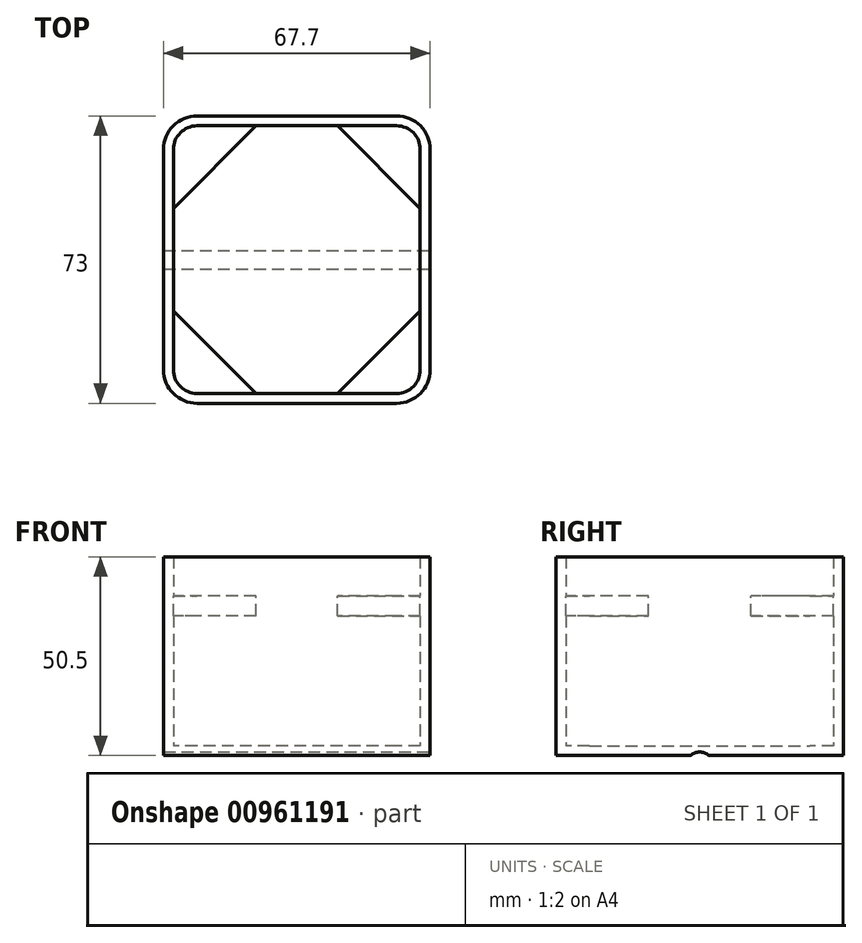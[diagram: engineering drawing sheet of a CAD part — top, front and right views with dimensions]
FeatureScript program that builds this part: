
annotation { "Feature Type Name" : "Feature", "Feature Type Description" : "" }
export const myFeature = defineFeature(function(context is Context, id is Id, definition is map)
    precondition{}
    {
        {
            var Q0;
            Q0=qCreatedBy(makeId("Top.planeOp"),FACE);
            var sketch = newSketch(context, id + "F0", { "sketchPlane" : qUnion([Q0])});
            skLineSegment(sketch, "E0.bottom", {"start": v(25.35, -36.5) * mm, "end": v(-25.35, -36.5) * mm});
            skLineSegment(sketch, "E0.top", {"start": v(25.35, 36.5) * mm, "end": v(-25.35, 36.5) * mm});
            skLineSegment(sketch, "E0.left", {"start": v(33.85, -28) * mm, "end": v(33.85, 28) * mm});
            skLineSegment(sketch, "E0.right", {"start": v(-33.85, -28) * mm, "end": v(-33.85, 28) * mm});
            skPoint(sketch, "E0.middle", {"position": v(0, 0) * mm});
            skPoint(sketch, "E1.visualSharp", {"position": v(-33.85, 36.5) * mm});
            skPoint(sketch, "E2.visualSharp", {"position": v(33.85, 36.5) * mm});
            skPoint(sketch, "E3.visualSharp", {"position": v(33.85, -36.5) * mm});
            skPoint(sketch, "E4.visualSharp", {"position": v(-33.85, -36.5) * mm});
            skArc(sketch, "E5.filletArc", {"start": v(-25.35, 36.5) * mm, "mid": v(-31.36, 34.01) * mm, "end": v(-33.85, 28) * mm});
            skArc(sketch, "E6.filletArc", {"start": v(33.85, 28) * mm, "mid": v(31.36, 34.01) * mm, "end": v(25.35, 36.5) * mm});
            skArc(sketch, "E7.filletArc", {"start": v(-33.85, -28) * mm, "mid": v(-31.36, -34.01) * mm, "end": v(-25.35, -36.5) * mm});
            skArc(sketch, "E8.filletArc", {"start": v(25.35, -36.5) * mm, "mid": v(31.36, -34.01) * mm, "end": v(33.85, -28) * mm});
            skSolve(sketch);
        }
        {
            var Q0;
            Q0=makeQuery(id+"F0.imprint","IMPRINT",FACE,{"disambiguationData":[TD([[makeQuery(id+"F0.imprint","IMPRINT",EDGE,{"derivedFrom":sQuery(id+"F0.wireOp",EDGE,"E0.bottom")}),-1.0]])]});
            extrude(context, id + "F1", {"entities" : qUnion([Q0]), "depth" : 2.5 * mm, "offsetDistance" : 25 * mm});
        }
        {
            var Q0;
            Q0=makeQuery(id+"F1.opExtrude","CAP_FACE",FACE,{"disambiguationData":[OSD([sQuery(id+"F0.wireOp",EDGE,"E0.bottom"),sQuery(id+"F0.wireOp",EDGE,"E0.top"),sQuery(id+"F0.wireOp",EDGE,"E0.left"),sQuery(id+"F0.wireOp",EDGE,"E0.right"),sQuery(id+"F0.wireOp",EDGE,"E1.filletArc"),sQuery(id+"F0.wireOp",EDGE,"E2.filletArc"),sQuery(id+"F0.wireOp",EDGE,"E3.filletArc"),sQuery(id+"F0.wireOp",EDGE,"E4.filletArc")])],"isStart":false});
            var sketch = newSketch(context, id + "F2", { "sketchPlane" : qUnion([Q0])});
            skLineSegment(sketch, "E9.bottom", {"start": v(25.35, -34) * mm, "end": v(-25.35, -34) * mm});
            skLineSegment(sketch, "E9.top", {"start": v(25.35, 34) * mm, "end": v(-25.35, 34) * mm});
            skLineSegment(sketch, "E9.left", {"start": v(31.35, -28) * mm, "end": v(31.35, 28) * mm});
            skLineSegment(sketch, "E9.right", {"start": v(-31.35, -28) * mm, "end": v(-31.35, 28) * mm});
            skPoint(sketch, "E9.middle", {"position": v(0, 0) * mm});
            skPoint(sketch, "E10.visualSharp", {"position": v(-31.35, 34) * mm});
            skPoint(sketch, "E11.visualSharp", {"position": v(31.35, 34) * mm});
            skPoint(sketch, "E12.visualSharp", {"position": v(-31.35, -34) * mm});
            skPoint(sketch, "E13.visualSharp", {"position": v(31.35, -34) * mm});
            skPoint(sketch, "E14", {"position": v(-22.35, 25) * mm});
            skPoint(sketch, "E15", {"position": v(22.35, 25) * mm});
            skPoint(sketch, "E16", {"position": v(22.35, -25) * mm});
            skPoint(sketch, "E17", {"position": v(-22.35, -25) * mm});
            skArc(sketch, "E18.filletArc", {"start": v(-25.35, 34) * mm, "mid": v(-29.6, 32.24) * mm, "end": v(-31.35, 28) * mm});
            skArc(sketch, "E19.filletArc", {"start": v(31.35, 28) * mm, "mid": v(29.6, 32.24) * mm, "end": v(25.35, 34) * mm});
            skArc(sketch, "E20.filletArc", {"start": v(25.35, -34) * mm, "mid": v(29.6, -32.24) * mm, "end": v(31.35, -28) * mm});
            skArc(sketch, "E21.filletArc", {"start": v(-31.35, -28) * mm, "mid": v(-29.6, -32.24) * mm, "end": v(-25.35, -34) * mm});
            skSolve(sketch);
        }
        {
            var Q0;
            Q0=makeQuery(id+"F2.imprint","IMPRINT",FACE,{"disambiguationData":[TD([[makeQuery(id+"F2.imprint","IMPRINT",EDGE,{"derivedFrom":sQuery(id+"F2.wireOp",EDGE,"E9.bottom")}),1.0]])]});
            extrude(context, id + "F3", {"entities" : qUnion([Q0]), "operationType" : NewBodyOperationType.ADD, "depth" : 38 * mm, "offsetDistance" : 25 * mm});
        }
        {
            var Q0;
            Q0=makeQuery(id+"F3.opExtrude","CAP_FACE",FACE,{"disambiguationData":[OSD([sQuery(id+"F0.wireOp",EDGE,"E0.bottom"),sQuery(id+"F0.wireOp",EDGE,"E0.top"),sQuery(id+"F0.wireOp",EDGE,"E0.left"),sQuery(id+"F0.wireOp",EDGE,"E0.right"),sQuery(id+"F0.wireOp",EDGE,"dvduAT8U-9z4F-e4AS-9eoL-lbGmKiJ1iybt"),sQuery(id+"F0.wireOp",EDGE,"aJOZrvJK-A2hF-QCfp-oE2e-V53GVGUSBUPk"),sQuery(id+"F0.wireOp",EDGE,"IG0yzDuE-LkIn-5tUI-d1jc-H29fERG7UsIG"),sQuery(id+"F0.wireOp",EDGE,"B1HQ0swq-clk5-EkSq-0daU-o4C5Dgl36Lca"),sQuery(id+"F0.wireOp",EDGE,"Mjkd7YmC-RiAe-4hFl-lhO9-aFGPjJMqciLP"),sQuery(id+"F2.wireOp",EDGE,"E9.bottom"),sQuery(id+"F2.wireOp",EDGE,"E9.top"),sQuery(id+"F2.wireOp",EDGE,"E9.left"),sQuery(id+"F2.wireOp",EDGE,"E9.right")])],"isStart":false});
            var sketch = newSketch(context, id + "F4", { "sketchPlane" : qUnion([Q0])});
            skLineSegment(sketch, "E22", {"start": v(-25.35, 34) * mm, "end": v(-10.36, 34) * mm});
            skLineSegment(sketch, "E23", {"start": v(-10.36, 34) * mm, "end": v(-31.35, 13.01) * mm});
            skLineSegment(sketch, "E24", {"start": v(-31.35, 13.01) * mm, "end": v(-31.36, 28) * mm});
            skLineSegment(sketch, "E25", {"start": v(25.36, 34) * mm, "end": v(10.37, 34) * mm});
            skLineSegment(sketch, "E26", {"start": v(10.37, 34) * mm, "end": v(31.35, 13) * mm});
            skLineSegment(sketch, "E27", {"start": v(31.35, 13) * mm, "end": v(31.36, 28) * mm});
            skLineSegment(sketch, "E28", {"start": v(-31.36, -28) * mm, "end": v(-31.35, -13.01) * mm});
            skLineSegment(sketch, "E29", {"start": v(-31.35, -13.01) * mm, "end": v(-10.36, -34) * mm});
            skLineSegment(sketch, "E30", {"start": v(-10.36, -34) * mm, "end": v(-25.35, -34) * mm});
            skLineSegment(sketch, "E31", {"start": v(31.36, -28) * mm, "end": v(31.35, -13) * mm});
            skLineSegment(sketch, "E32", {"start": v(31.35, -13) * mm, "end": v(10.37, -34) * mm});
            skLineSegment(sketch, "E33", {"start": v(10.37, -34) * mm, "end": v(25.36, -34) * mm});
            skPoint(sketch, "E34.visualSharp", {"position": v(-31.36, 34.01) * mm});
            skArc(sketch, "E34.filletArc", {"start": v(-25.35, 34) * mm, "mid": v(-29.6, 32.25) * mm, "end": v(-31.36, 28) * mm});
            skPoint(sketch, "E35.visualSharp", {"position": v(31.37, 34) * mm});
            skArc(sketch, "E35.filletArc", {"start": v(31.36, 28) * mm, "mid": v(29.6, 32.24) * mm, "end": v(25.36, 34) * mm});
            skPoint(sketch, "E36.visualSharp", {"position": v(-31.36, -34.01) * mm});
            skArc(sketch, "E36.filletArc", {"start": v(-31.36, -28) * mm, "mid": v(-29.6, -32.25) * mm, "end": v(-25.35, -34) * mm});
            skPoint(sketch, "E37.visualSharp", {"position": v(31.37, -34) * mm});
            skArc(sketch, "E37.filletArc", {"start": v(25.36, -34) * mm, "mid": v(29.6, -32.24) * mm, "end": v(31.36, -28) * mm});
            skSolve(sketch);
        }
        {
            var Q0;
            {var subQ0=sQuery(id+"F4.wireOp",EDGE,"E23");Q0=makeQuery(id+"F4.imprint","IMPRINT",FACE,{"disambiguationData":[TD([[makeQuery(id+"F4.imprint","IMPRINT",EDGE,{"derivedFrom":subQ0}),-1.0]])]});}
            var Q1;
            {var subQ0=sQuery(id+"F4.wireOp",EDGE,"E26");Q1=makeQuery(id+"F4.imprint","IMPRINT",FACE,{"disambiguationData":[TD([[makeQuery(id+"F4.imprint","IMPRINT",EDGE,{"derivedFrom":subQ0}),1.0]])]});}
            var Q2;
            {var subQ6=sQuery(id+"F4.wireOp",EDGE,"E32");Q2=makeQuery(id+"F4.imprint","IMPRINT",FACE,{"disambiguationData":[TD([[makeQuery(id+"F4.imprint","IMPRINT",EDGE,{"derivedFrom":subQ6}),1.0]])]});}
            var Q3;
            {var subQ0=sQuery(id+"F4.wireOp",EDGE,"E29");Q3=makeQuery(id+"F4.imprint","IMPRINT",FACE,{"disambiguationData":[TD([[makeQuery(id+"F4.imprint","IMPRINT",EDGE,{"derivedFrom":subQ0}),-1.0]])]});}
            extrude(context, id + "F5", {"entities" : qUnion([Q0, Q1, Q2, Q3]), "operationType" : NewBodyOperationType.ADD, "oppositeDirection" : true, "depth" : 5 * mm, "offsetDistance" : 25 * mm});
        }
        {
            var Q0;
            {var subQ0=sQuery(id+"F0.wireOp",EDGE,"B1HQ0swq-clk5-EkSq-0daU-o4C5Dgl36Lca");var subQ1=sQuery(id+"F0.wireOp",EDGE,"E0.left");Q0=makeQuery(id+"FCPAo5pOO8WpCQz_1.boolean.opBoolean","MERGE",FACE,{"derivedFrom":[makeQuery(id+"F3.boolean.opBoolean","MERGE",FACE,{"derivedFrom":[makeQuery(id+"F1.opExtrude","SWEPT_FACE",FACE,{"disambiguationData":[OSD([subQ1,subQ0])]}),makeQuery(id+"F3.opExtrude","SWEPT_FACE",FACE,{"disambiguationData":[OSD([subQ1,subQ0])]})]}),makeQuery(id+"FCPAo5pOO8WpCQz_1.opExtrude","SWEPT_FACE",FACE,{"disambiguationData":[OSD([sQuery(id+"FqFhjzdwi1l4fy1_1.wireOp",EDGE,"z4WKYeDy-sNTH-M1Wg-ofNn-E9ZkuAjsT8kv.right")])]})]});}
            var sketch = newSketch(context, id + "F6", { "sketchPlane" : qUnion([Q0])});
            skCircle(sketch, "E38", {"center": v(0, -2.61) * mm, "radius": 3.5 * mm});
            skSolve(sketch);
        }
        {
            var Q0;
            {var subQ0=sQuery(id+"F6.wireOp",EDGE,"E38");var subQ1=makeQuery(id+"F1.opExtrude","CAP_EDGE",EDGE,{"disambiguationData":[OSD([sQuery(id+"F0.wireOp",EDGE,"E0.left"),sQuery(id+"F0.wireOp",EDGE,"B1HQ0swq-clk5-EkSq-0daU-o4C5Dgl36Lca")])],"isStart":true});var subQ2=makeQuery(id+"F6.imprint","INTERSECT",VERTEX,{"disambiguationData":[OD(0.0)],"derivedFrom":[subQ1,subQ0]});Q0=makeQuery(id+"F6.imprint","IMPRINT",FACE,{"disambiguationData":[TD([[makeQuery(id+"F6.imprint","IMPRINT",EDGE,{"disambiguationData":[TD([[subQ2,1.0]])],"derivedFrom":subQ0}),1.0]])]});}
            extrude(context, id + "F7", {"entities" : qUnion([Q0]), "operationType" : NewBodyOperationType.REMOVE, "endBound" : BoundingType.THROUGH_ALL, "oppositeDirection" : true, "depth" : 25 * mm, "offsetDistance" : 25 * mm});
        }
        {
            var Q0;
            {var subQ0=sQuery(id+"F2.wireOp",EDGE,"E20.filletArc");var subQ1=sQuery(id+"F2.wireOp",EDGE,"E9.left");var subQ2=sQuery(id+"F2.wireOp",EDGE,"E21.filletArc");var subQ3=sQuery(id+"F2.wireOp",EDGE,"E9.right");var subQ4=sQuery(id+"F2.wireOp",EDGE,"E9.bottom");var subQ5=sQuery(id+"F2.wireOp",EDGE,"E19.filletArc");var subQ6=sQuery(id+"F2.wireOp",EDGE,"E18.filletArc");var subQ7=sQuery(id+"F2.wireOp",EDGE,"E9.top");Q0=makeQuery(id+"F5.boolean.opBoolean","MERGE",FACE,{"derivedFrom":[makeQuery(id+"F3.opExtrude","CAP_FACE",FACE,{"disambiguationData":[OSD([sQuery(id+"F0.wireOp",EDGE,"E0.bottom"),sQuery(id+"F0.wireOp",EDGE,"E0.top"),sQuery(id+"F0.wireOp",EDGE,"E0.left"),sQuery(id+"F0.wireOp",EDGE,"E0.right"),sQuery(id+"F0.wireOp",EDGE,"E5.filletArc"),sQuery(id+"F0.wireOp",EDGE,"E6.filletArc"),sQuery(id+"F0.wireOp",EDGE,"E7.filletArc"),sQuery(id+"F0.wireOp",EDGE,"E8.filletArc"),subQ4,subQ7,subQ1,subQ3,subQ6,subQ5,subQ0,subQ2])],"isStart":false}),makeQuery(id+"F5.opExtrude","CAP_FACE",FACE,{"disambiguationData":[OSD([subQ7,subQ3,subQ6,sQuery(id+"F4.wireOp",EDGE,"E23")])],"isStart":true}),makeQuery(id+"F5.opExtrude","CAP_FACE",FACE,{"disambiguationData":[OSD([subQ1,subQ5,sQuery(id+"F4.wireOp",EDGE,"E25"),sQuery(id+"F4.wireOp",EDGE,"E26")])],"isStart":true}),makeQuery(id+"F5.opExtrude","CAP_FACE",FACE,{"disambiguationData":[OSD([subQ4,subQ3,subQ2,sQuery(id+"F4.wireOp",EDGE,"E29")])],"isStart":true}),makeQuery(id+"F5.opExtrude","CAP_FACE",FACE,{"disambiguationData":[OSD([subQ1,subQ0,sQuery(id+"F4.wireOp",EDGE,"E32"),sQuery(id+"F4.wireOp",EDGE,"E33")])],"isStart":true})]});}
            var sketch = newSketch(context, id + "F8", { "sketchPlane" : qUnion([Q0])});
            skLineSegment(sketch, "E39.bottom", {"start": v(25.35, 34) * mm, "end": v(-25.35, 34) * mm});
            skLineSegment(sketch, "E39.top", {"start": v(25.35, -34) * mm, "end": v(-25.35, -34) * mm});
            skLineSegment(sketch, "E39.left", {"start": v(31.35, 28) * mm, "end": v(31.35, -28) * mm});
            skLineSegment(sketch, "E39.right", {"start": v(-31.35, 28) * mm, "end": v(-31.35, -28) * mm});
            skPoint(sketch, "E39.middle", {"position": v(0, 0) * mm});
            skPoint(sketch, "E40.visualSharp", {"position": v(-31.35, 34) * mm});
            skArc(sketch, "E40.filletArc", {"start": v(-25.35, 34) * mm, "mid": v(-29.6, 32.24) * mm, "end": v(-31.35, 28) * mm});
            skPoint(sketch, "E41.visualSharp", {"position": v(31.35, 34) * mm});
            skArc(sketch, "E41.filletArc", {"start": v(31.35, 28) * mm, "mid": v(29.6, 32.24) * mm, "end": v(25.35, 34) * mm});
            skPoint(sketch, "E42.visualSharp", {"position": v(-31.35, -34) * mm});
            skArc(sketch, "E42.filletArc", {"start": v(-31.35, -28) * mm, "mid": v(-29.6, -32.24) * mm, "end": v(-25.35, -34) * mm});
            skPoint(sketch, "E43.visualSharp", {"position": v(31.35, -34) * mm});
            skArc(sketch, "E43.filletArc", {"start": v(25.35, -34) * mm, "mid": v(29.6, -32.24) * mm, "end": v(31.35, -28) * mm});
            skSolve(sketch);
        }
        {
            var Q0;
            {var subQ3=sQuery(id+"F8.wireOp",EDGE,"E40.filletArc");Q0=makeQuery(id+"F8.imprint","IMPRINT",FACE,{"disambiguationData":[TD([[makeQuery(id+"F8.imprint","IMPRINT",EDGE,{"derivedFrom":subQ3}),-1.0]])]});}
            extrude(context, id + "F9", {"entities" : qUnion([Q0]), "operationType" : NewBodyOperationType.ADD, "depth" : 10 * mm, "offsetDistance" : 25 * mm});
        }
    });
